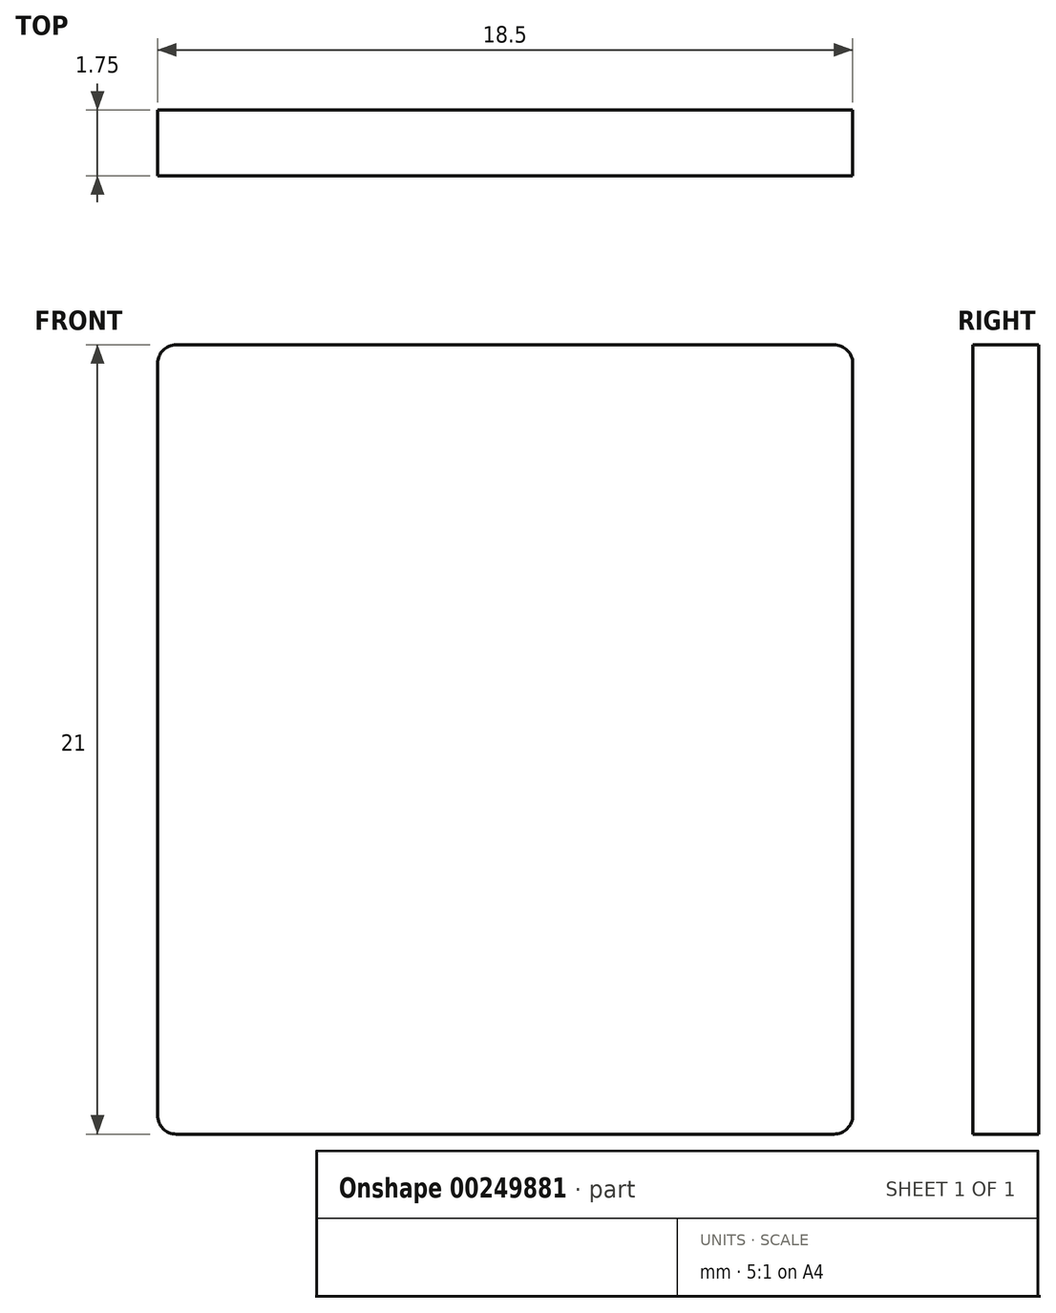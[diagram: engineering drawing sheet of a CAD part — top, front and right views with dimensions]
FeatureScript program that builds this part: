
annotation { "Feature Type Name" : "Feature", "Feature Type Description" : "" }
export const myFeature = defineFeature(function(context is Context, id is Id, definition is map)
    precondition{}
    {
        {
            var Q0;
            Q0=qCreatedBy(makeId("Front.planeOp"),FACE);
            var sketch = newSketch(context, id + "F0", { "sketchPlane" : qUnion([Q0])});
            skLineSegment(sketch, "E0.bottom", {"start": v(8.75, -10.5) * mm, "end": v(-8.75, -10.5) * mm});
            skLineSegment(sketch, "E0.top", {"start": v(8.75, 10.5) * mm, "end": v(-8.75, 10.5) * mm});
            skLineSegment(sketch, "E0.left", {"start": v(9.25, -10) * mm, "end": v(9.25, 10) * mm});
            skLineSegment(sketch, "E0.right", {"start": v(-9.25, -10) * mm, "end": v(-9.25, 10) * mm});
            skPoint(sketch, "E0.middle", {"position": v(0, 0) * mm});
            skPoint(sketch, "E1.visualSharp", {"position": v(-9.25, 10.5) * mm});
            skArc(sketch, "E1.filletArc", {"start": v(-8.75, 10.5) * mm, "mid": v(-9.1, 10.35) * mm, "end": v(-9.25, 10) * mm});
            skPoint(sketch, "E2.visualSharp", {"position": v(9.25, 10.5) * mm});
            skArc(sketch, "E2.filletArc", {"start": v(9.25, 10) * mm, "mid": v(9.1, 10.35) * mm, "end": v(8.75, 10.5) * mm});
            skPoint(sketch, "E3.visualSharp", {"position": v(9.25, -10.5) * mm});
            skArc(sketch, "E3.filletArc", {"start": v(8.75, -10.5) * mm, "mid": v(9.1, -10.35) * mm, "end": v(9.25, -10) * mm});
            skPoint(sketch, "E4.visualSharp", {"position": v(-9.25, -10.5) * mm});
            skArc(sketch, "E4.filletArc", {"start": v(-9.25, -10) * mm, "mid": v(-9.1, -10.35) * mm, "end": v(-8.75, -10.5) * mm});
            skSolve(sketch);
        }
        {
            var Q0;
            Q0 = qSketchRegion(id + "F0", true);
            extrude(context, id + "F1", {"entities" : qUnion([Q0]), "depth" : 1.75 * mm});
        }
    });
